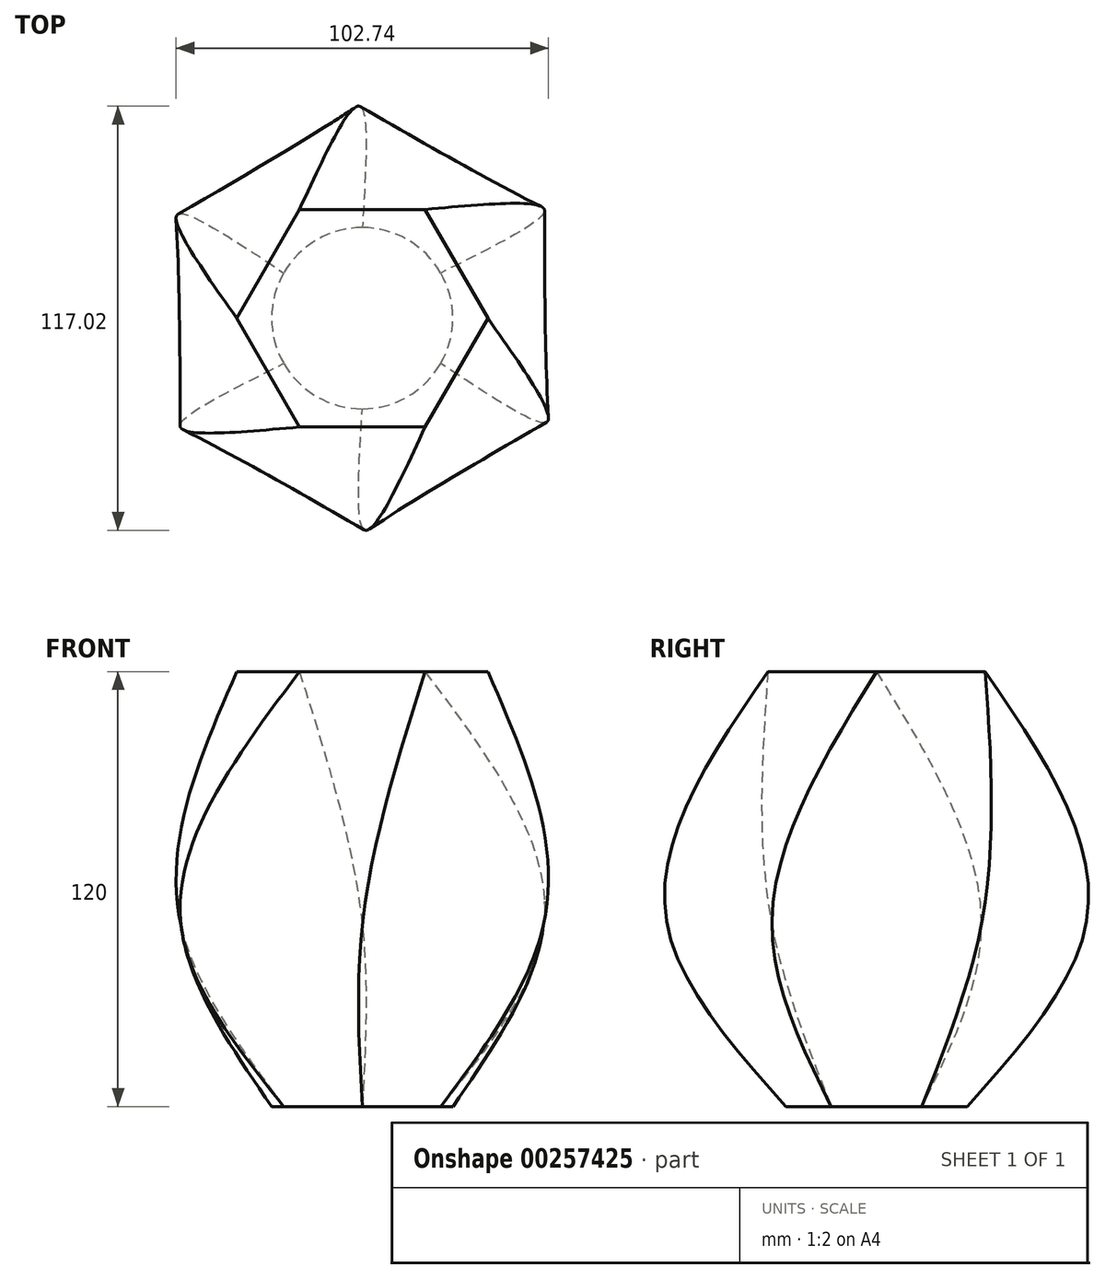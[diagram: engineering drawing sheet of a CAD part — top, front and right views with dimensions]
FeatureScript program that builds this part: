
annotation { "Feature Type Name" : "Feature", "Feature Type Description" : "" }
export const myFeature = defineFeature(function(context is Context, id is Id, definition is map)
    precondition{}
    {
        {
            var Q0;
            Q0=qCreatedBy(makeId("Top.planeOp"),FACE);
            var sketch = newSketch(context, id + "F0", { "sketchPlane" : qUnion([Q0])});
            skCircle(sketch, "E0.cCircle", {"center": v(0, 0) * mm, "radius": 30 * mm, "construction": true});
            skLineSegment(sketch, "E0.0", {"start": v(-17.32, 30) * mm, "end": v(17.32, 30) * mm});
            skLineSegment(sketch, "E0.1", {"start": v(17.32, 30) * mm, "end": v(34.64, 0) * mm});
            skLineSegment(sketch, "E0.2", {"start": v(34.64, 0) * mm, "end": v(17.32, -30) * mm});
            skLineSegment(sketch, "E0.3", {"start": v(17.32, -30) * mm, "end": v(-17.32, -30) * mm});
            skLineSegment(sketch, "E0.4", {"start": v(-17.32, -30) * mm, "end": v(-34.64, 0) * mm});
            skLineSegment(sketch, "E0.5", {"start": v(-34.64, 0) * mm, "end": v(-17.32, 30) * mm});
            skPoint(sketch, "E0.0.midPoint", {"position": v(0, 30) * mm});
            skSolve(sketch);
        }
        {
            var Q0;
            Q0=qCreatedBy(makeId("Top.planeOp"),FACE);
            cPlane(context, id + "F1", {"entities" : qUnion([Q0]), "cplaneType" : CPlaneType.OFFSET, "offset" : 70 * mm, "oppositeDirection" : true, "width" : 150 * mm, "height" : 150 * mm});
        }
        {
            var Q0;
            Q0=qCreatedBy(id+"F1.planeOp",FACE);
            var sketch = newSketch(context, id + "F2", { "sketchPlane" : qUnion([Q0])});
            skCircle(sketch, "E1.cCircle", {"center": v(0, 0) * mm, "radius": 50 * mm, "construction": true});
            skLineSegment(sketch, "E1.0", {"start": v(50, 28.87) * mm, "end": v(50, -28.87) * mm});
            skLineSegment(sketch, "E1.1", {"start": v(50, -28.87) * mm, "end": v(0, -57.74) * mm});
            skLineSegment(sketch, "E1.2", {"start": v(0, -57.74) * mm, "end": v(-50, -28.87) * mm});
            skLineSegment(sketch, "E1.3", {"start": v(-50, -28.87) * mm, "end": v(-50, 28.87) * mm});
            skLineSegment(sketch, "E1.4", {"start": v(-50, 28.87) * mm, "end": v(0, 57.74) * mm});
            skLineSegment(sketch, "E1.5", {"start": v(0, 57.74) * mm, "end": v(50, 28.87) * mm});
            skPoint(sketch, "E1.0.midPoint", {"position": v(50, 0) * mm});
            skSolve(sketch);
        }
        {
            var Q0;
            Q0=qCreatedBy(id+"F1.planeOp",FACE);
            cPlane(context, id + "F3", {"entities" : qUnion([Q0]), "cplaneType" : CPlaneType.OFFSET, "offset" : 50 * mm, "oppositeDirection" : true, "width" : 150 * mm, "height" : 150 * mm});
        }
        {
            var Q0;
            Q0=qCreatedBy(id+"F3.planeOp",FACE);
            var sketch = newSketch(context, id + "F4", { "sketchPlane" : qUnion([Q0])});
            skCircle(sketch, "E2", {"center": v(0, 0) * mm, "radius": 25 * mm});
            skSolve(sketch);
        }
        {
            var Q0;
            Q0=makeQuery(id+"F0.imprint","IMPRINT",FACE,{"disambiguationData":[TD([[makeQuery(id+"F0.imprint","IMPRINT",EDGE,{"derivedFrom":sQuery(id+"F0.wireOp",EDGE,"E0.0")}),-1.0]])]});
            var Q1;
            Q1=makeQuery(id+"F2.imprint","IMPRINT",FACE,{"disambiguationData":[TD([[makeQuery(id+"F2.imprint","IMPRINT",EDGE,{"derivedFrom":sQuery(id+"F2.wireOp",EDGE,"E1.0")}),-1.0]])]});
            var Q2;
            Q2=makeQuery(id+"F4.imprint","IMPRINT",FACE,{"disambiguationData":[TD([[makeQuery(id+"F4.imprint","IMPRINT",EDGE,{"derivedFrom":sQuery(id+"F4.wireOp",EDGE,"E2")}),1.0]])]});
            loft(context, id + "F5", {"sheetProfilesArray" : [{ "sheetProfileEntities" : qUnion([Q0]) }, { "sheetProfileEntities" : qUnion([Q1]) }, { "sheetProfileEntities" : qUnion([Q2]) }]});
        }
    });
